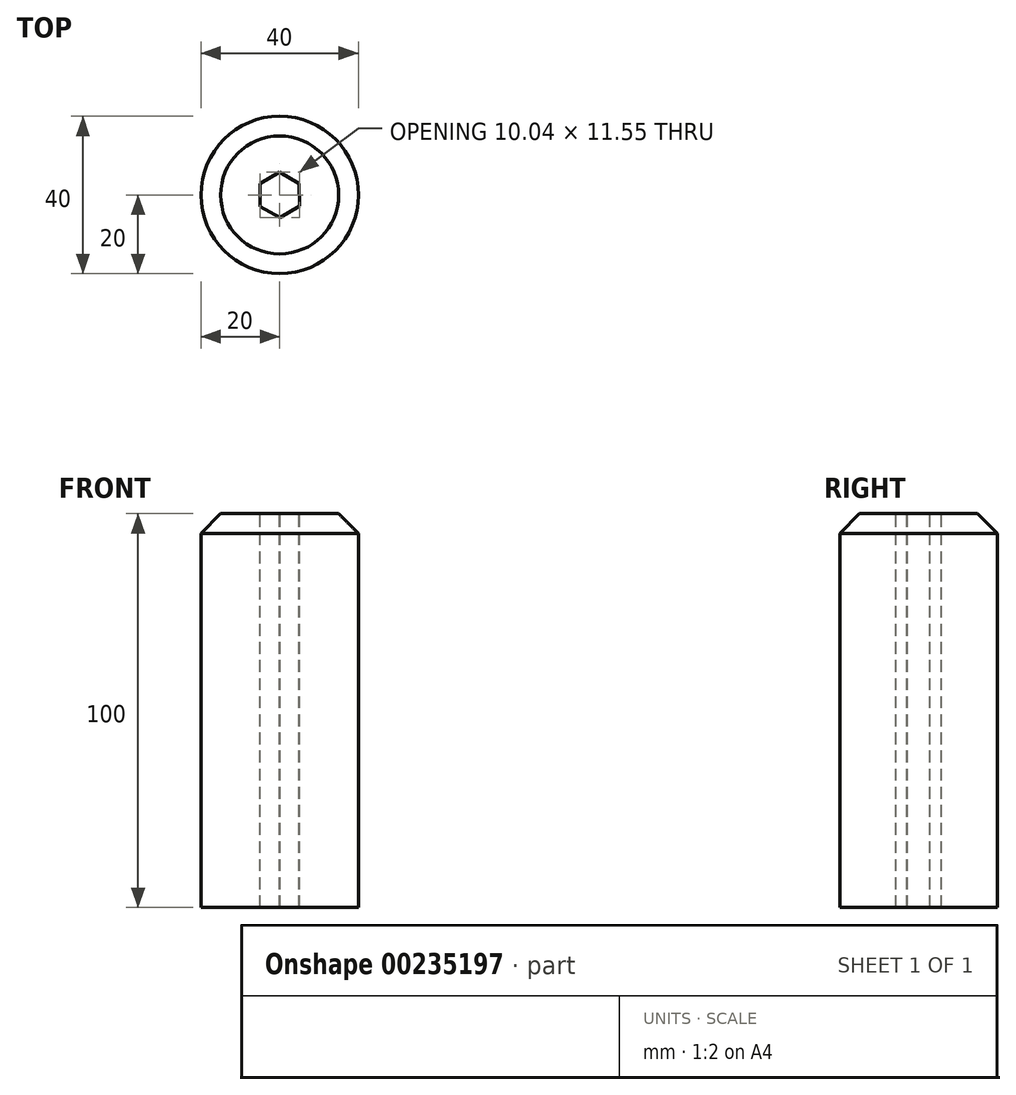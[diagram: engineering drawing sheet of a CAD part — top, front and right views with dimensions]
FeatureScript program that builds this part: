
annotation { "Feature Type Name" : "Feature", "Feature Type Description" : "" }
export const myFeature = defineFeature(function(context is Context, id is Id, definition is map)
    precondition{}
    {
        {
            var Q0;
            Q0=qCreatedBy(makeId("Top.planeOp"),FACE);
            var sketch = newSketch(context, id + "F0", { "sketchPlane" : qUnion([Q0])});
            skCircle(sketch, "E0", {"center": v(0, 0) * mm, "radius": 20 * mm});
            skSolve(sketch);
        }
        {
            var Q0;
            Q0=makeQuery(id+"F0.imprint","IMPRINT",FACE,{"disambiguationData":[TD([[makeQuery(id+"F0.imprint","IMPRINT",EDGE,{"derivedFrom":sQuery(id+"F0.wireOp",EDGE,"E0")}),1.0]])]});
            extrude(context, id + "F1", {"entities" : qUnion([Q0]), "depth" : 100 * mm, "offsetDistance" : 25 * mm});
        }
        {
            var Q0;
            Q0=makeQuery(id+"F1.opExtrude","CAP_EDGE",EDGE,{"disambiguationData":[OSD([sQuery(id+"F0.wireOp",EDGE,"E0")])],"isStart":false});
            chamfer(context, id + "F2", {"entities" : qUnion([Q0]), "width" : 5 * mm, "tangentPropagation" : true});
        }
        {
            var Q0;
            Q0=makeQuery(id+"F1.opExtrude","CAP_FACE",FACE,{"disambiguationData":[OSD([sQuery(id+"F0.wireOp",EDGE,"E0")])],"isStart":false});
            var sketch = newSketch(context, id + "F3", { "sketchPlane" : qUnion([Q0])});
            skCircle(sketch, "E1.cCircle", {"center": v(0, 0) * mm, "radius": 5 * mm, "construction": true});
            skLineSegment(sketch, "E1.0", {"start": v(5.02, -2.85) * mm, "end": v(0.04, -5.77) * mm});
            skLineSegment(sketch, "E1.1", {"start": v(0.04, -5.77) * mm, "end": v(-4.98, -2.92) * mm});
            skLineSegment(sketch, "E1.2", {"start": v(-4.98, -2.92) * mm, "end": v(-5.02, 2.85) * mm});
            skLineSegment(sketch, "E1.3", {"start": v(-5.02, 2.85) * mm, "end": v(-0.04, 5.77) * mm});
            skLineSegment(sketch, "E1.4", {"start": v(-0.04, 5.77) * mm, "end": v(4.98, 2.92) * mm});
            skLineSegment(sketch, "E1.5", {"start": v(4.98, 2.92) * mm, "end": v(5.02, -2.85) * mm});
            skPoint(sketch, "E1.0.midPoint", {"position": v(2.53, -4.31) * mm});
            skSolve(sketch);
        }
        {
            var Q0;
            Q0=makeQuery(id+"F3.imprint","IMPRINT",FACE,{"disambiguationData":[TD([[makeQuery(id+"F3.imprint","IMPRINT",EDGE,{"derivedFrom":sQuery(id+"F3.wireOp",EDGE,"E1.0")}),-1.0]])]});
            extrude(context, id + "F4", {"entities" : qUnion([Q0]), "operationType" : NewBodyOperationType.REMOVE, "endBound" : BoundingType.THROUGH_ALL, "oppositeDirection" : true, "depth" : 25 * mm, "offsetDistance" : 25 * mm});
        }
    });
